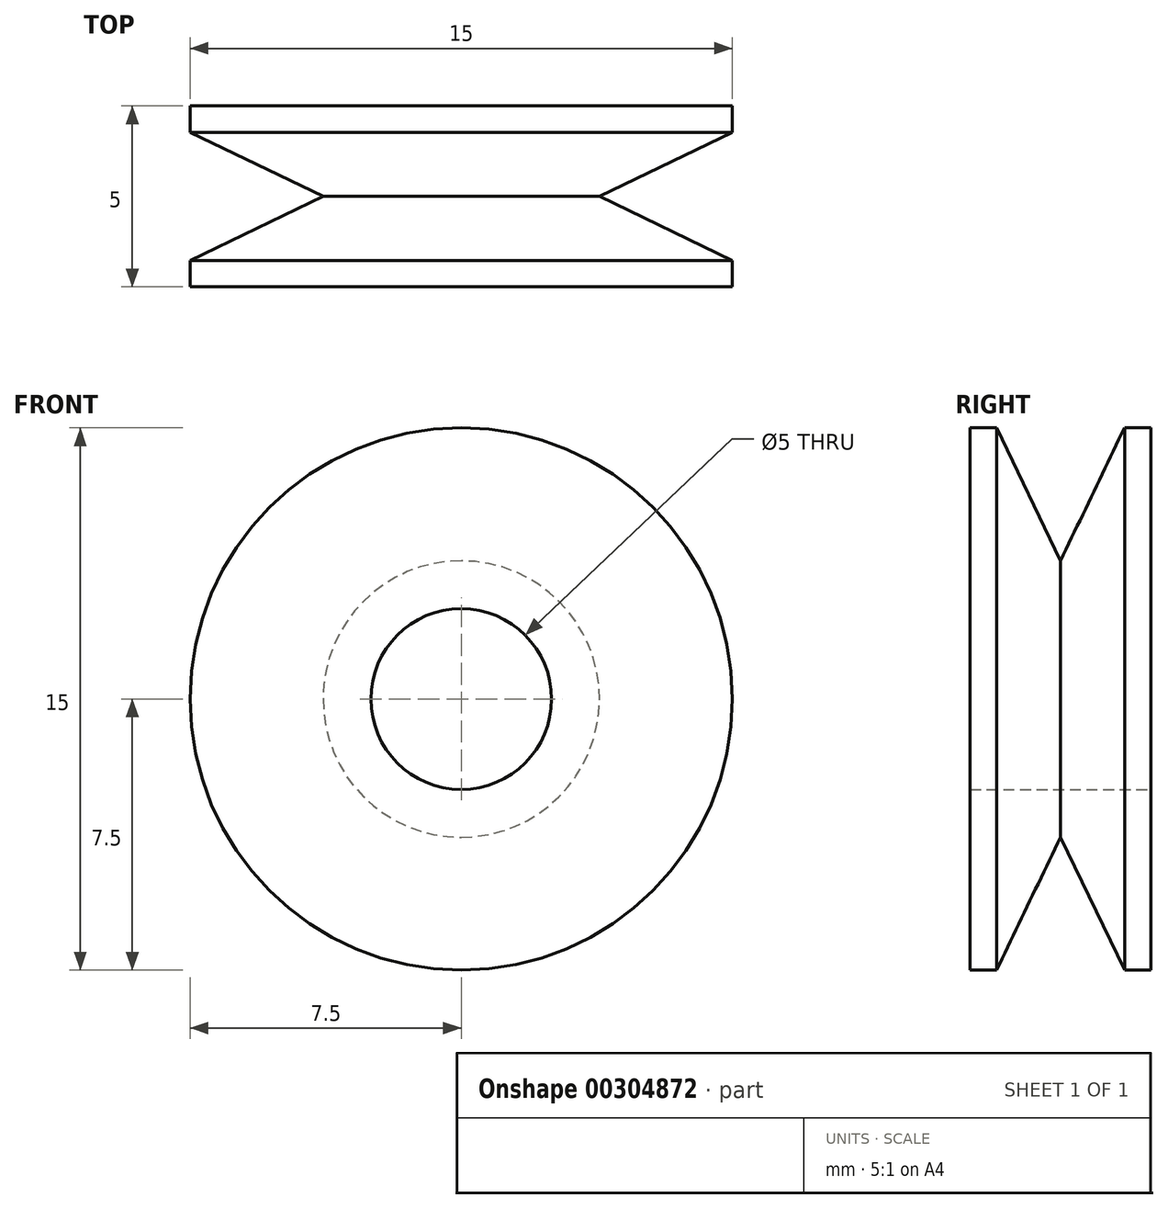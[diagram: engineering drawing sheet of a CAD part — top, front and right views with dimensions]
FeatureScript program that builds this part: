
annotation { "Feature Type Name" : "Feature", "Feature Type Description" : "" }
export const myFeature = defineFeature(function(context is Context, id is Id, definition is map)
    precondition{}
    {
        {
            var Q0;
            Q0=qCreatedBy(makeId("Front.planeOp"),FACE);
            var sketch = newSketch(context, id + "F0", { "sketchPlane" : qUnion([Q0])});
            skPoint(sketch, "E0", {"position": v(-20, 0) * mm});
            skPoint(sketch, "E1", {"position": v(20, 0) * mm});
            skCircle(sketch, "E2", {"center": v(-20, 0) * mm, "radius": 7.5 * mm});
            skCircle(sketch, "E3", {"center": v(20, 0) * mm, "radius": 7.5 * mm});
            skPoint(sketch, "E4", {"position": v(0, 0) * mm});
            skPoint(sketch, "E5", {"position": v(0, 10) * mm});
            skCircle(sketch, "E6", {"center": v(0, 10) * mm, "radius": 2.35 * mm});
            skCircle(sketch, "E7", {"center": v(-20, 0) * mm, "radius": 2.5 * mm});
            skCircle(sketch, "E8", {"center": v(20, 0) * mm, "radius": 2.5 * mm});
            skSolve(sketch);
        }
        {
            var Q0;
            Q0=qCreatedBy(makeId("Front.planeOp"),FACE);
            var sketch = newSketch(context, id + "F1", { "sketchPlane" : qUnion([Q0])});
            skPoint(sketch, "E9", {"position": v(-30, 0) * mm});
            skPoint(sketch, "E10", {"position": v(30, 0) * mm});
            skFitSpline(sketch, "E11", {"points": [v(-30, 0) * mm, v(0, 14.81) * mm, v(30, 0) * mm, v(0, -13.65) * mm, v(-30, 0) * mm]});
            skSolve(sketch);
        }
        {
            var Q0;
            Q0=makeQuery(id+"F0.imprint","IMPRINT",FACE,{"disambiguationData":[TD([[makeQuery(id+"F0.imprint","IMPRINT",EDGE,{"derivedFrom":sQuery(id+"F0.wireOp",EDGE,"E2")}),1.0]])]});
            extrude(context, id + "F2", {"entities" : qUnion([Q0]), "depth" : 5 * mm});
        }
        {
            var Q0;
            Q0=qCreatedBy(makeId("Right.planeOp"),FACE);
            cPlane(context, id + "F3", {"entities" : qUnion([Q0]), "cplaneType" : CPlaneType.OFFSET, "offset" : 20 * mm, "oppositeDirection" : true, "width" : 150 * mm, "height" : 150 * mm});
        }
        {
            var Q0;
            Q0=qCreatedBy(id+"F3.planeOp",FACE);
            var sketch = newSketch(context, id + "F4", { "sketchPlane" : qUnion([Q0])});
            skPoint(sketch, "E12", {"position": v(-2.5, 0) * mm});
            skLineSegment(sketch, "E13", {"start": v(-2.5, 0) * mm, "end": v(-2.5, 10.67) * mm});
            skLineSegment(sketch, "E14", {"start": v(0, 7.56) * mm, "end": v(-4.83, 7.56) * mm});
            skPoint(sketch, "E15", {"position": v(-0.7, 7.56) * mm});
            skPoint(sketch, "E16", {"position": v(-4.3, 7.56) * mm});
            skPoint(sketch, "E17", {"position": v(-2.5, 3.82) * mm});
            skLineSegment(sketch, "E18", {"start": v(-0.7, 7.56) * mm, "end": v(-2.5, 3.82) * mm});
            skLineSegment(sketch, "E19", {"start": v(-4.3, 7.56) * mm, "end": v(-2.5, 3.82) * mm});
            skLineSegment(sketch, "E20", {"start": v(0, 0) * mm, "end": v(-7.02, 0) * mm});
            skSolve(sketch);
        }
        {
            var Q0;
            {var subQ0=sQuery(id+"F4.wireOp",EDGE,"E19");Q0=makeQuery(id+"F4.imprint","IMPRINT",FACE,{"disambiguationData":[TD([[makeQuery(id+"F4.imprint","IMPRINT",EDGE,{"derivedFrom":subQ0}),1.0]])]});}
            var Q1;
            {var subQ0=sQuery(id+"F4.wireOp",EDGE,"E18");Q1=makeQuery(id+"F4.imprint","IMPRINT",FACE,{"disambiguationData":[TD([[makeQuery(id+"F4.imprint","IMPRINT",EDGE,{"derivedFrom":subQ0}),-1.0]])]});}
            var Q2;
            Q2=sQuery(id+"F4.wireOp",EDGE,"E20");
            revolve(context, id + "F5", {"operationType" : NewBodyOperationType.REMOVE, "entities" : qUnion([Q0, Q1]), "axis" : qUnion([Q2]), "revolveType" : RevolveType.FULL, "oppositeDirection" : true});
        }
    });
